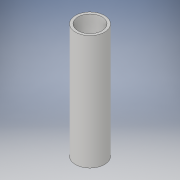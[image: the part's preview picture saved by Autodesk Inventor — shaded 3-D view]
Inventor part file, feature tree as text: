
AUTODESK INVENTOR PART (.ipt)
format: ipt  version: 2019 (Build 230136000, 136)  size: 98,816 bytes
history: native  units: mm
features: extrude x2, sketch x2, other x1
ambient origin geometry x8: Origin, YZ Plane, XZ Plane, XY Plane, X Axis, Y Axis, Z Axis, Center Point
bodies: Body1 (feature_tree)
feature tree (5):
  other  "Sólido1"
  extrude  "Extrusión1"  Depth=30.0mm TaperAngle=0.0deg
  extrude  "Extrusión2"  Depth=20.0mm TaperAngle=0.0deg
  sketch  "Boceto1"  dims[d0=7.6mm d1=30.0mm d2=0.0mm]
  sketch  "Boceto2"  dims[d3=6.3mm d4=20.0mm d5=0.0mm]
